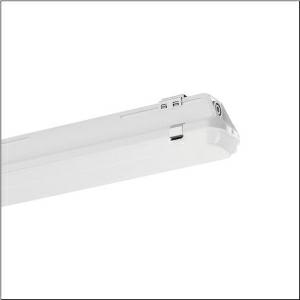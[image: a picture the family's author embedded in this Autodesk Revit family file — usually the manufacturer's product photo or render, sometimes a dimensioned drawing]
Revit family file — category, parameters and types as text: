
# Revit family: monsun_21_emergency_51fb10dp437c3h
name_source: partatom
category: Lighting Fixtures
units: mm (PartAtom-declared; Revit-internal decimal feet)

## family parameters
Cut with Voids When Loaded = No
Host = Face
Light Source = No
Part Type = Normal
Room Calculation Point = No
Round Connector Dimension = Use Diameter
Shared = No

## types (1)
- --- (1 x LED, 3860 lm, 25.5 W, 4000K)
    Apparent Load = 26 VA
    CIE Flux Codes = 47 77 93 94 100
    Color Rendering = 80
    Color Temperature = 4000K
    Default Elevation = 1800 mm
    Description = Monsun 21 emergency, damp-proof luminaire, chain hanger, primary optical cover: enclosure, of PMMA, light emission: direct distribution, primary light characteristic: symmetric, installation type: vertical mounting, horizontal mounting, surface-mounted, suspended mounting, LED, rated luminous flux: 3.860lm, luminous efficacy: 178lm/W, light colour: 840, colour temperature: 4000K, control gear: DALI 2, with terminal, 5+3-pole, max. 2.5mm², mains connection: 220..240V, AC, 50/60Hz, rated input power: 26W, control gear: single battery element, battery: LiFePO4, 9Ah, housing, of glass-fibre reinforced polyester, uncoated, bright grey, incl. chain hanger, length: 1.590mm, width: 90mm, height: 88mm, clip for enclosure, of stainless steel (V2A), ceiling mounting element, of stainless steel (V2A), chain hanger, of stainless steel (V2A), protection rating (complete): IP66, insulation class (complete): insulation class I (protective earthing), certification: CE, UKCA, protection symbol: D, impact resistance: IK04, permissible operating ambient temperature: +5..+25°C, standard: EN 50419, EN 60598-2-1, EN 60598-2-22, corresponds to IFS (International Featured Standards) requirements for safety and quality in the food industry, for indoor or canopied outdoor use, no direct snow, no direct sun, no direct rain, LABS conformity tested according to VDMA 24364:2018-05, contact your sales advisor before using the luminaires in applications with unclear chemical exposure, large temperature fluctuations or condensation-forming humidity, packaging unit: 1 piece
    Height = 89 mm
    Lamp = 1 x LED
    Lamp Light Flux = 3860 lm
    Lamp Power = 25.5 W
    Lamp count = 1
    Length = 1590 mm
    Luminous efficacy = 151 lm/W
    Manufacturer = Siteco
    ModVariant = No
    Model = 51FB10DP437C3H
    Mounting Place = Ceiling
    Mounting Type = Surface mounted
    Number of Poles = 1
    OnlyDefault = Yes
    Power Factor = 1
    Product Name = Monsun 21 emergency
    Product group = damp-proof luminaire
    ProductGroupID = 300
    Protection Class = Protection class I
    Protection Degree = IP 66
    RLX_Detail_Level = 1
    RLX_Emergency_Light_Flux = 0 lm
    RLX_Emergency_Type = 0
    RLX_Emergency_Type_DB = No
    RlxData = <blob elided: 92189 chars, md5=8c1354d4>
    Socket = socket
    Standby Power = 0 W
    System Light Flux = 3860 lm
    System Power = 26 W
    Type Comments = : luminous flux: 100 % | dim-lin: 254 | 144 mA
    Type Image = l_1319656.jpg
    URL = http://relux.com
    VarID = @adj_038281
    Voltage = 0 V
    Weight = 0.00 kg
    Width = 90 mm

## geometry (parser evidence)
native form markers: Blend x4, Sweep x14
no freeform markers — native parametric forms only
